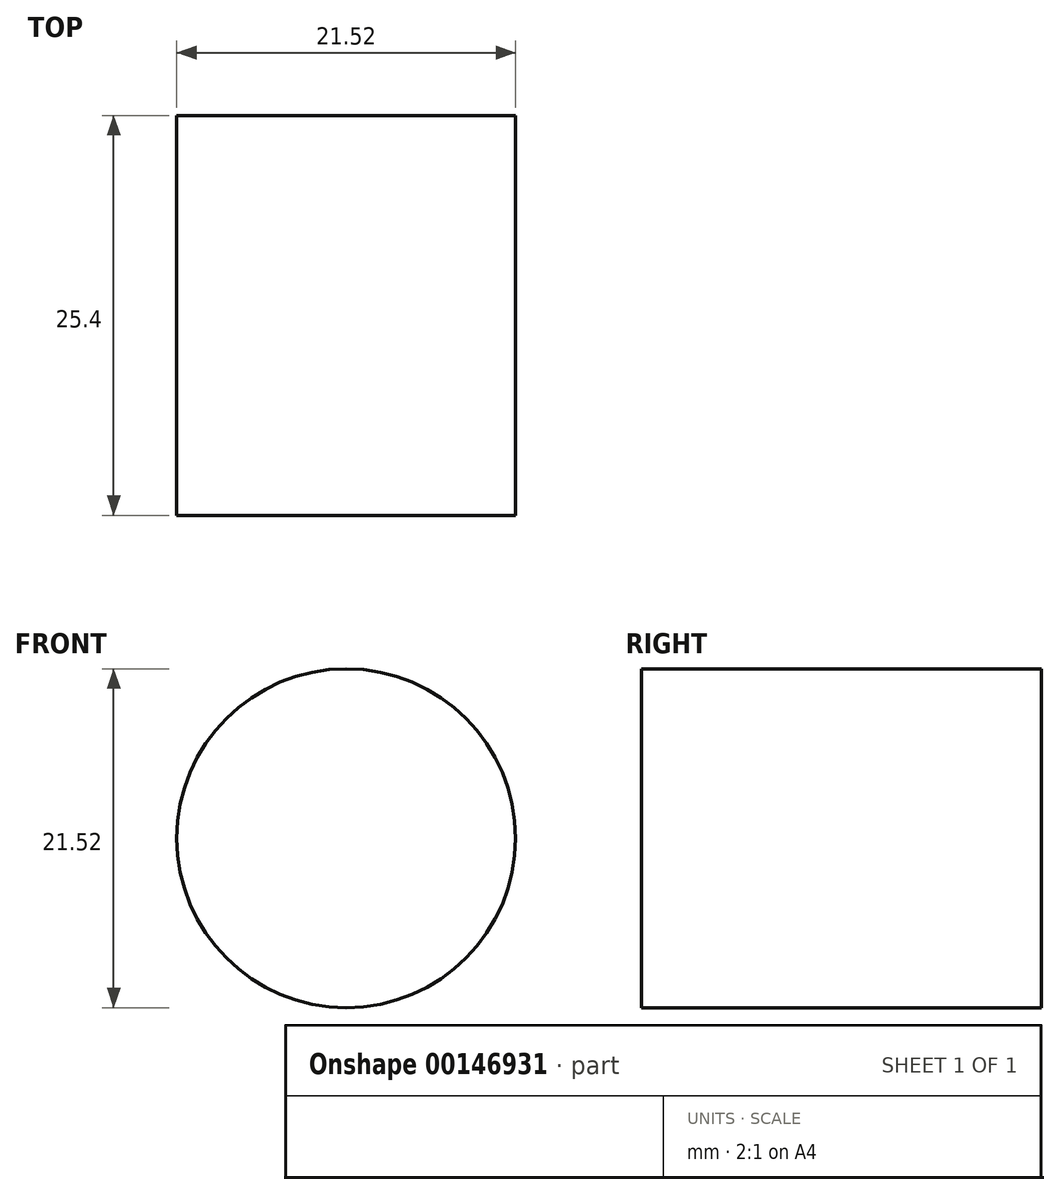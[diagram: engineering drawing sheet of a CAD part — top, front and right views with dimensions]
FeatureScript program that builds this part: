
annotation { "Feature Type Name" : "Feature", "Feature Type Description" : "" }
export const myFeature = defineFeature(function(context is Context, id is Id, definition is map)
    precondition{}
    {
        {
            var Q0;
            Q0=qCreatedBy(makeId("Front.planeOp"),FACE);
            var sketch = newSketch(context, id + "F0", { "sketchPlane" : qUnion([Q0])});
            skCircle(sketch, "E0", {"center": v(0, 0) * mm, "radius": 10.76 * mm});
            skSolve(sketch);
        }
        {
            var Q0;
            Q0 = qSketchRegion(id + "F0", true);
            extrude(context, id + "F1", {"entities" : qUnion([Q0]), "depth" : 25.4 * mm});
        }
        {
            var Q0;
            Q0 = qSketchRegion(id + "F0", true);
            extrude(context, id + "F2", {"entities" : qUnion([Q0]), "operationType" : NewBodyOperationType.ADD, "depth" : 25.4 * mm});
        }
    });
